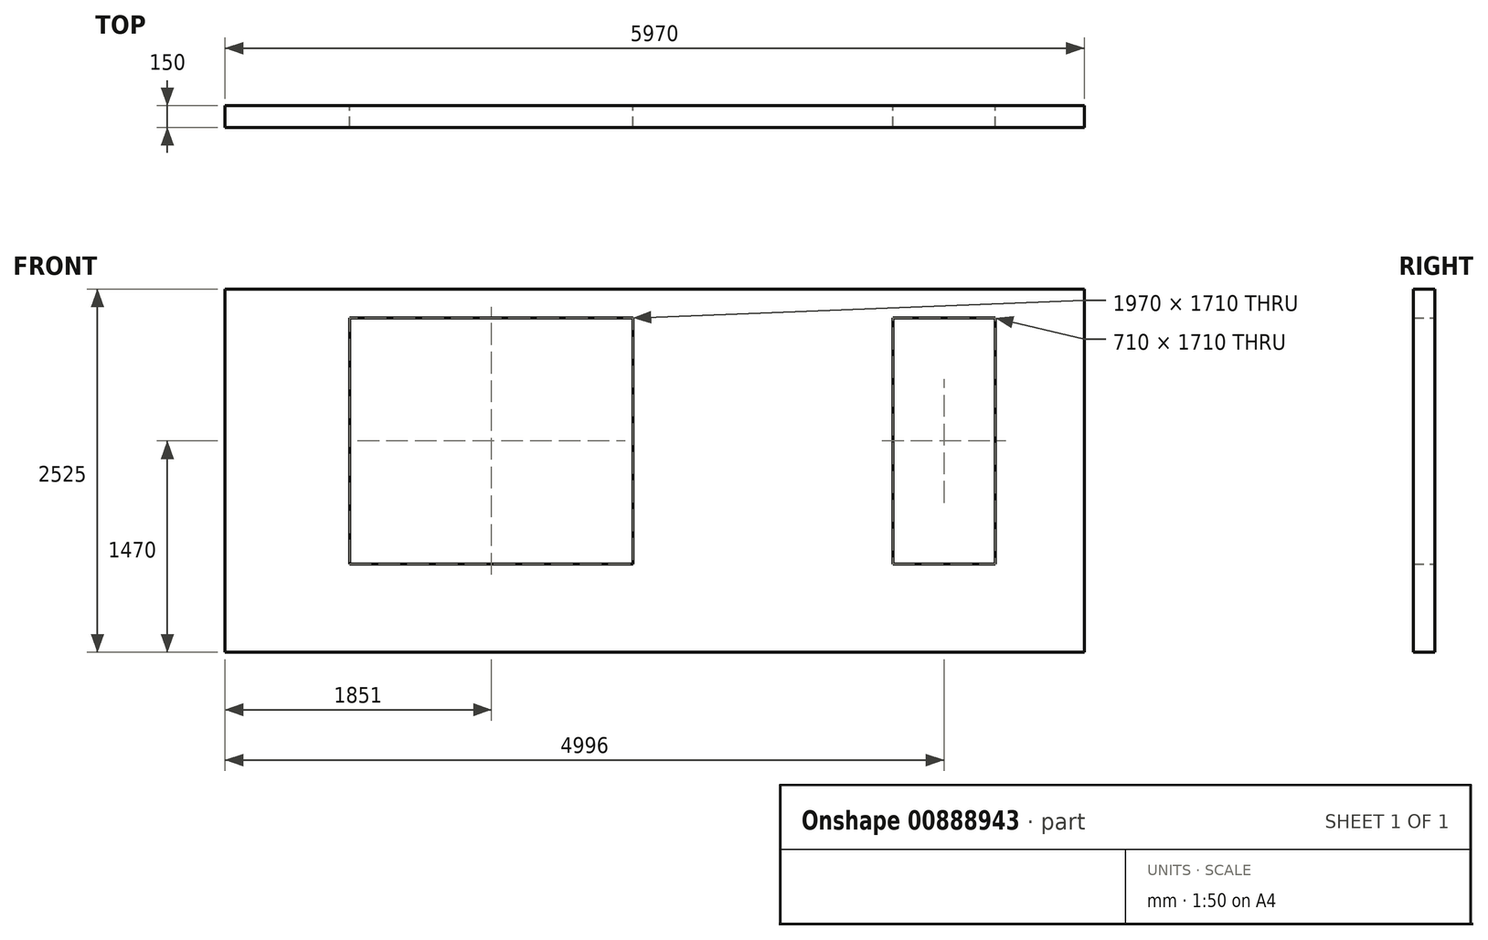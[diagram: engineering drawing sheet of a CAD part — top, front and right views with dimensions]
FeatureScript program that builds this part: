
annotation { "Feature Type Name" : "Feature", "Feature Type Description" : "" }
export const myFeature = defineFeature(function(context is Context, id is Id, definition is map)
    precondition{}
    {
        {
            var Q0;
            Q0=qCreatedBy(makeId("Front.planeOp"),FACE);
            var sketch = newSketch(context, id + "F0", { "sketchPlane" : qUnion([Q0])});
            skLineSegment(sketch, "E0.bottom", {"start": v(0, 0) * mm, "end": v(5970, 0) * mm});
            skLineSegment(sketch, "E0.top", {"start": v(0, 2525) * mm, "end": v(5970, 2525) * mm});
            skLineSegment(sketch, "E0.left", {"start": v(0, 0) * mm, "end": v(0, 2525) * mm});
            skLineSegment(sketch, "E0.right", {"start": v(5970, 0) * mm, "end": v(5970, 2525) * mm});
            skLineSegment(sketch, "E1.bottom", {"start": v(0, 0) * mm, "end": v(866, 0) * mm});
            skLineSegment(sketch, "E1.top", {"start": v(0, 615) * mm, "end": v(866, 615) * mm});
            skLineSegment(sketch, "E1.left", {"start": v(0, 0) * mm, "end": v(0, 615) * mm});
            skLineSegment(sketch, "E1.right", {"start": v(866, 0) * mm, "end": v(866, 615) * mm});
            skLineSegment(sketch, "E2.bottom", {"start": v(866, 615) * mm, "end": v(2836, 615) * mm});
            skLineSegment(sketch, "E2.top", {"start": v(866, 2325) * mm, "end": v(2836, 2325) * mm});
            skLineSegment(sketch, "E2.left", {"start": v(866, 615) * mm, "end": v(866, 2325) * mm});
            skLineSegment(sketch, "E2.right", {"start": v(2836, 615) * mm, "end": v(2836, 2325) * mm});
            skLineSegment(sketch, "E3.bottom", {"start": v(5970, 0) * mm, "end": v(5351, 0) * mm});
            skLineSegment(sketch, "E3.top", {"start": v(5970, 615) * mm, "end": v(5351, 615) * mm});
            skLineSegment(sketch, "E3.left", {"start": v(5970, 0) * mm, "end": v(5970, 615) * mm});
            skLineSegment(sketch, "E3.right", {"start": v(5351, 0) * mm, "end": v(5351, 615) * mm});
            skLineSegment(sketch, "E4.bottom", {"start": v(5351, 615) * mm, "end": v(4641, 615) * mm});
            skLineSegment(sketch, "E4.top", {"start": v(5351, 2325) * mm, "end": v(4641, 2325) * mm});
            skLineSegment(sketch, "E4.left", {"start": v(5351, 615) * mm, "end": v(5351, 2325) * mm});
            skLineSegment(sketch, "E4.right", {"start": v(4641, 615) * mm, "end": v(4641, 2325) * mm});
            skSolve(sketch);
        }
        {
            var Q0;
            {var subQ4=sQuery(id+"F0.wireOp",EDGE,"E0.top");Q0=makeQuery(id+"F0.imprint","IMPRINT",FACE,{"disambiguationData":[TD([[makeQuery(id+"F0.imprint","IMPRINT",EDGE,{"derivedFrom":subQ4}),-1.0]])]});}
            var Q1;
            {var subQ4=sQuery(id+"F0.wireOp",EDGE,"E3.top");Q1=makeQuery(id+"F0.imprint","IMPRINT",FACE,{"disambiguationData":[TD([[makeQuery(id+"F0.imprint","IMPRINT",EDGE,{"derivedFrom":subQ4}),1.0]])]});}
            var Q2;
            {var subQ4=sQuery(id+"F0.wireOp",EDGE,"E1.top");Q2=makeQuery(id+"F0.imprint","IMPRINT",FACE,{"disambiguationData":[TD([[makeQuery(id+"F0.imprint","IMPRINT",EDGE,{"derivedFrom":subQ4}),-1.0]])]});}
            extrude(context, id + "F1", {"entities" : qUnion([Q0, Q1, Q2]), "depth" : 150 * mm, "offsetDistance" : 25 * mm});
        }
    });
